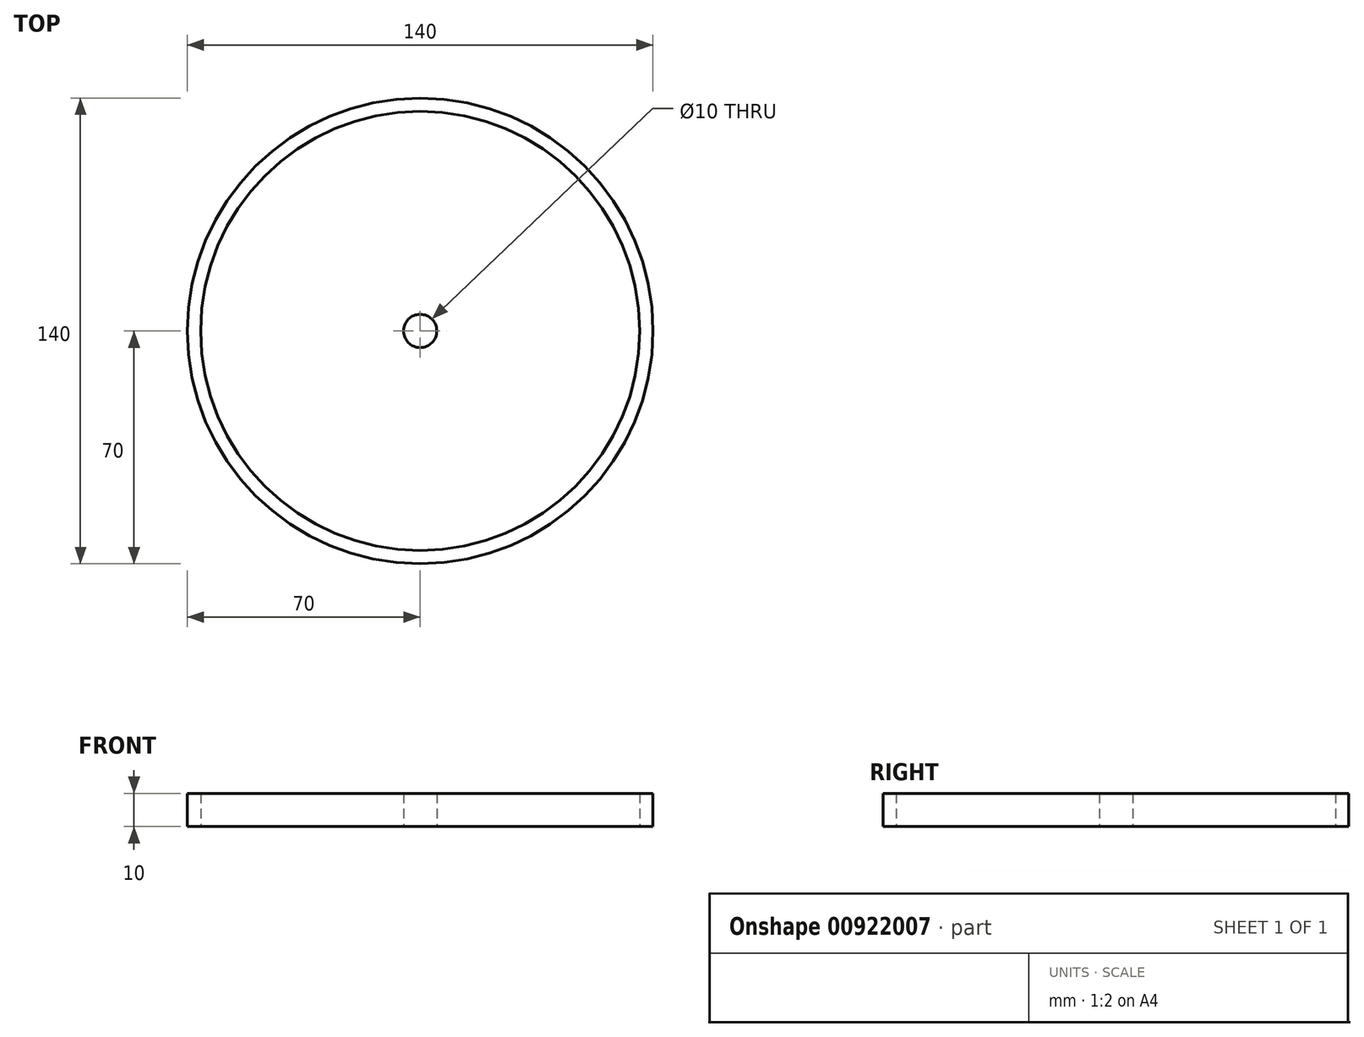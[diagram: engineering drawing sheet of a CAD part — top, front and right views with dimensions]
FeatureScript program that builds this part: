
annotation { "Feature Type Name" : "Feature", "Feature Type Description" : "" }
export const myFeature = defineFeature(function(context is Context, id is Id, definition is map)
    precondition{}
    {
        {
            var Q0;
            Q0=qCreatedBy(makeId("Top.planeOp"),FACE);
            var sketch = newSketch(context, id + "F0", { "sketchPlane" : qUnion([Q0])});
            skCircle(sketch, "E0", {"center": v(0, 0) * mm, "radius": 70 * mm});
            skSolve(sketch);
        }
        {
            var Q0;
            Q0 = qSketchRegion(id + "F0", true);
            extrude(context, id + "F1", {"entities" : qUnion([Q0]), "depth" : 10 * mm, "offsetDistance" : 25 * mm});
        }
        {
            var Q0;
            Q0=qCreatedBy(makeId("Top.planeOp"),FACE);
            var sketch = newSketch(context, id + "F2", { "sketchPlane" : qUnion([Q0])});
            skCircle(sketch, "E1", {"center": v(0, 0) * mm, "radius": 66 * mm});
            skCircle(sketch, "E2", {"center": v(0, 0) * mm, "radius": 5 * mm});
            skSolve(sketch);
        }
        {
            var Q0;
            Q0 = qSketchRegion(id + "F2", true);
            extrude(context, id + "F3", {"entities" : qUnion([Q0]), "depth" : 10 * mm, "offsetDistance" : 25 * mm});
        }
    });
